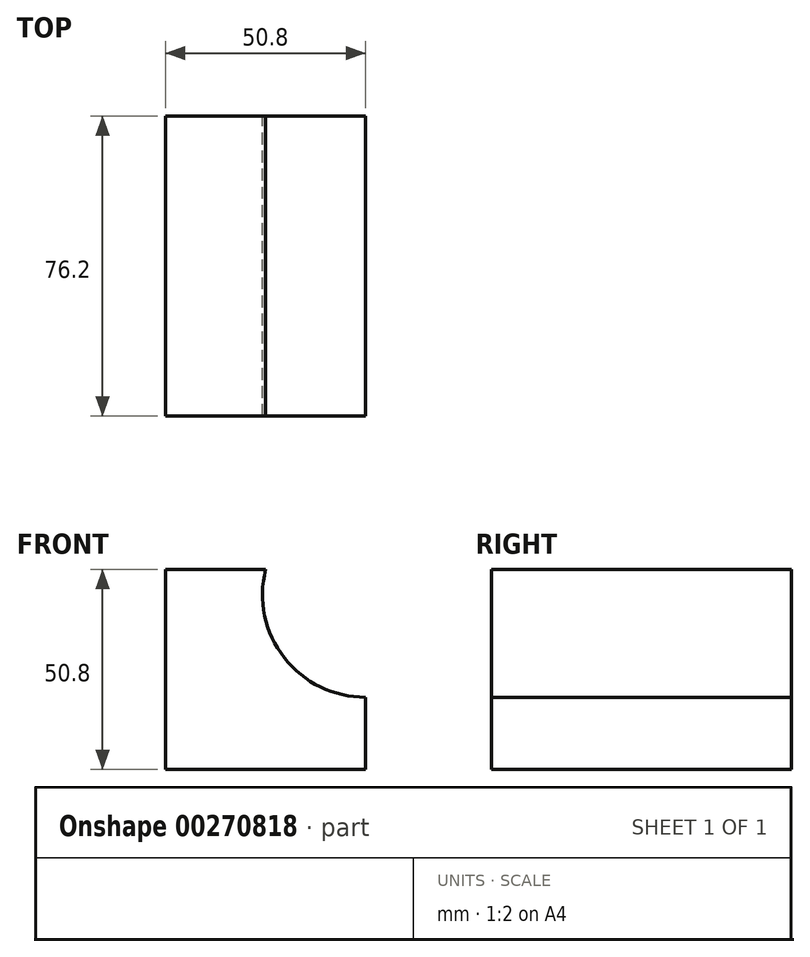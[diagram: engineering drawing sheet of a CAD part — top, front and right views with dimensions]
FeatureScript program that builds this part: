
annotation { "Feature Type Name" : "Feature", "Feature Type Description" : "" }
export const myFeature = defineFeature(function(context is Context, id is Id, definition is map)
    precondition{}
    {
        {
            var Q0;
            Q0=qCreatedBy(makeId("Front.planeOp"),FACE);
            var sketch = newSketch(context, id + "F0", { "sketchPlane" : qUnion([Q0])});
            skLineSegment(sketch, "E0", {"start": v(-63.59, 0) * mm, "end": v(-63.59, 50.8) * mm});
            skLineSegment(sketch, "E1", {"start": v(-63.59, 50.8) * mm, "end": v(-38.19, 50.8) * mm});
            skArc(sketch, "E2", {"start": v(-38.19, 50.8) * mm, "mid": v(-33.42, 28.36) * mm, "end": v(-12.79, 18.34) * mm});
            skLineSegment(sketch, "E3", {"start": v(-12.79, 18.34) * mm, "end": v(-12.79, 0) * mm});
            skLineSegment(sketch, "E4", {"start": v(-12.79, 0) * mm, "end": v(-63.59, 0) * mm});
            skSolve(sketch);
        }
        {
            var Q0;
            Q0 = qSketchRegion(id + "F0", true);
            extrude(context, id + "F1", {"entities" : qUnion([Q0]), "depth" : 76.2 * mm});
        }
    });
